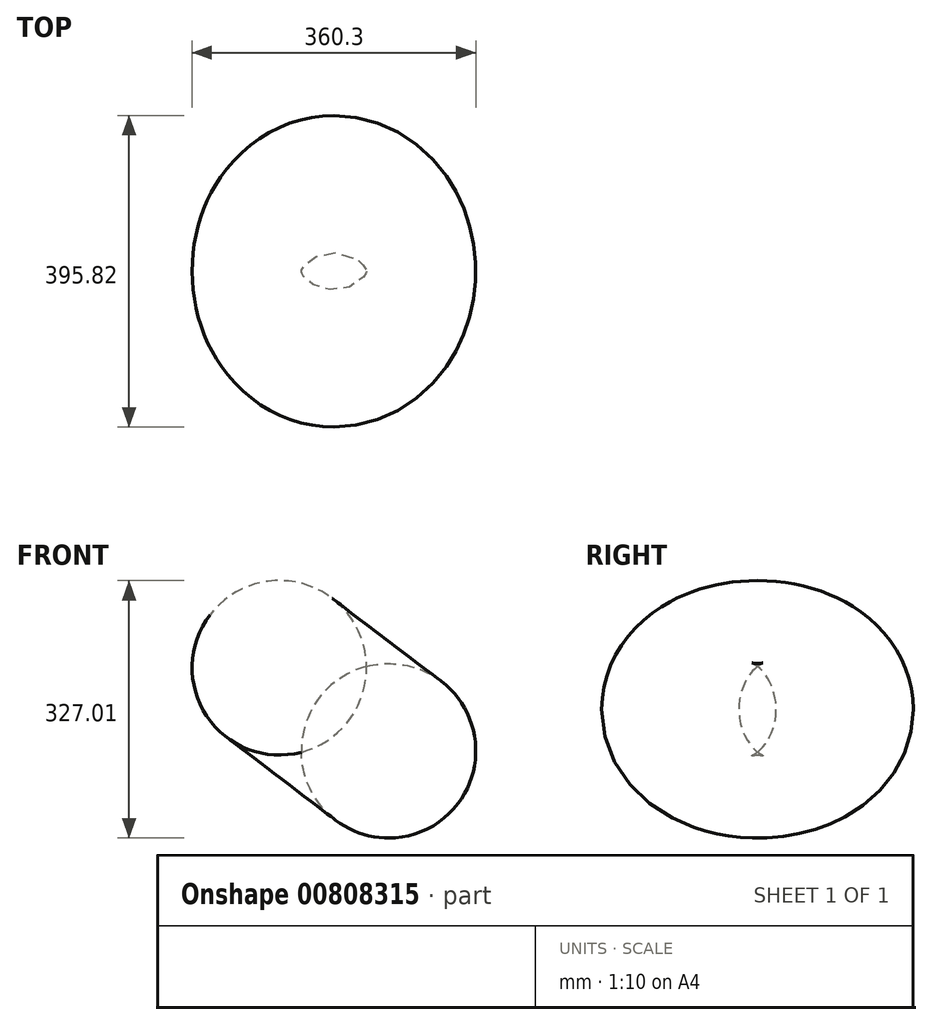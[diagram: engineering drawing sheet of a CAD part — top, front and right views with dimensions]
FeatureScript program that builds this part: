
annotation { "Feature Type Name" : "Feature", "Feature Type Description" : "" }
export const myFeature = defineFeature(function(context is Context, id is Id, definition is map)
    precondition{}
    {
        {
            var Q0;
            Q0=qCreatedBy(makeId("Front.planeOp"),FACE);
            var sketch = newSketch(context, id + "F0", { "sketchPlane" : qUnion([Q0])});
            skCircle(sketch, "E0", {"center": v(-38.33, 41.38) * mm, "radius": 110.8 * mm});
            skLineSegment(sketch, "E1", {"start": v(-107.34, 75.58) * mm, "end": v(-10.4, -65.84) * mm});
            skLineSegment(sketch, "E2", {"start": v(-10.4, -65.84) * mm, "end": v(86.88, 62.15) * mm});
            skSolve(sketch);
        }
        {
            var Q0;
            {var subQ0=sQuery(id+"F0.wireOp",EDGE,"E2");var subQ1=sQuery(id+"F0.wireOp",EDGE,"E0");var subQ2=makeQuery(id+"F0.imprint","INTERSECT",VERTEX,{"disambiguationData":[OD(0.0)],"derivedFrom":[subQ1,subQ0]});Q0=makeQuery(id+"F0.imprint","IMPRINT",FACE,{"disambiguationData":[TD([[makeQuery(id+"F0.imprint","IMPRINT",EDGE,{"disambiguationData":[TD([[subQ2,-1.0]])],"derivedFrom":subQ1}),1.0]])]});}
            var Q1;
            Q1=sQuery(id+"F0.wireOp",EDGE,"E2");
            revolve(context, id + "F1", {"surfaceOperationType" : NewSurfaceOperationType.NEW, "entities" : qUnion([Q0]), "axis" : qUnion([Q1]), "revolveType" : RevolveType.FULL});
        }
    });
